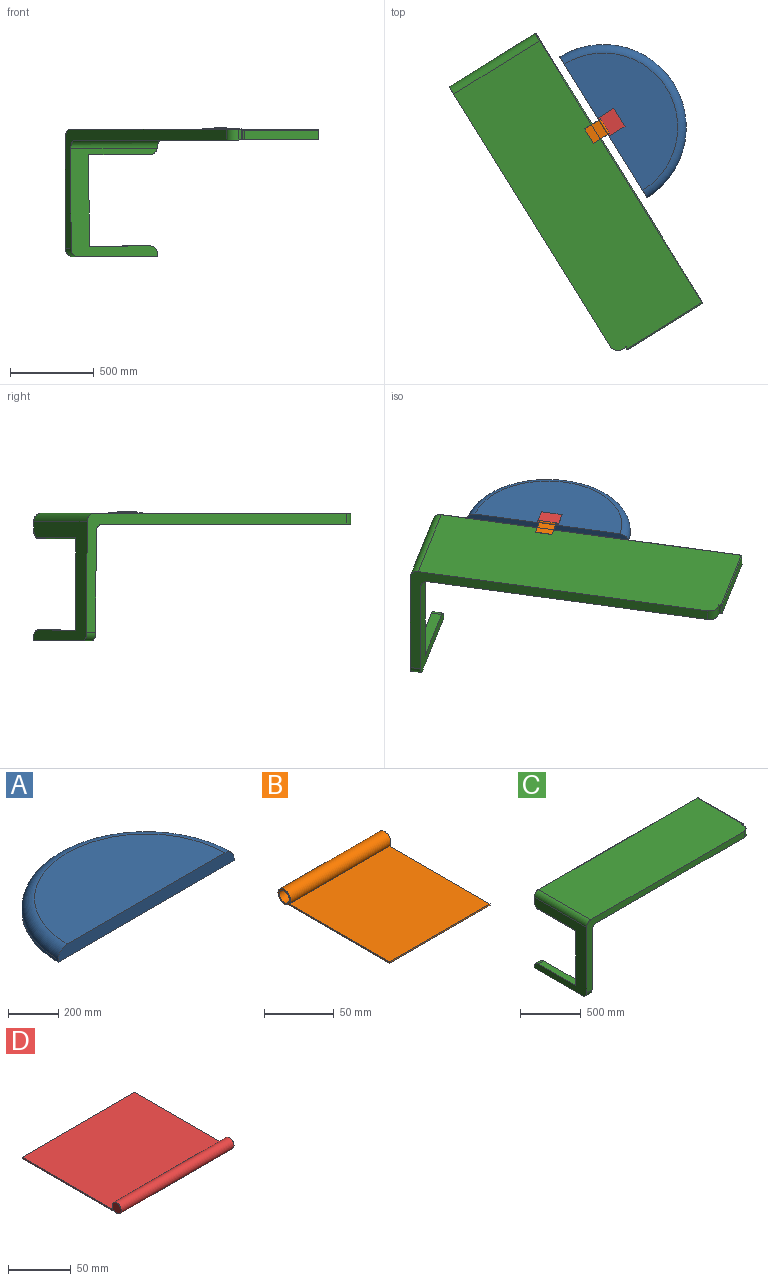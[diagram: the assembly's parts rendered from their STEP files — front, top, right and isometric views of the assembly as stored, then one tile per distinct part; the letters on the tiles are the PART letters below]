
ASSEMBLY  parts=4 mates=3
PART A: 5 faces, bbox 1072.2x536.1x63.5 mm
  f0: plane 990.6x63.5mm, normal (0,-1,0), area 61795.5mm2, adj f1,f2,f3,f4
  f1: cylinder r=495.3mm len=990.6mm, axis (0,0,1), area 19761.6mm2, adj f0,f2,f4
  f2: plane 990.6x495.3mm, normal (0,0,-1), area 385351mm2, adj f0,f1
  f3: plane 889x444.5mm, normal (0,0,1), area 310358.3mm2, adj f0,f4
  f4: torus R=444.5mm, axis (0,0,1), area 119538.1mm2, adj f0,f1,f3
PART B: 7 faces, bbox 101.6x113x12.7 mm
  f0: plane 101.6x101.6mm, normal (0,0,1), area 10322.6mm2, adj f1,f4,f5,f6
  f1: plane 101.6x1.27mm, normal (0,-1,0), area 129mm2, adj f0,f2,f5,f6
  f2: plane 102.87x101.6mm, normal (0,0,-1), area 10451.6mm2, adj f1,f4,f5,f6
  f3: cylinder r=5.08mm len=101.6mm, axis (1,0,0), area 3242.9mm2, adj f5,f6
  f4: cylinder r=6.35mm len=101.6mm, axis (1,0,0), area 3870.6mm2, adj f0,f2,f5,f6
  f5: plane 113.03x12.7mm, normal (-1,0,0), area 175.4mm2, adj f0,f1,f2,f3,f4
  f6: plane 113.03x12.7mm, normal (1,0,0), area 175.4mm2, adj f0,f1,f2,f3,f4
PART C: 33 faces, bbox 1902.8x613.8x766.2 mm
  f0: plane 63.5x30.48mm, normal (1,0,0), area 1618.4mm2, adj f6,f7,f13,f20,f32
  f1: plane 647.7x609.6mm, normal (1,0,0), area 129635.4mm2, adj f3,f4,f5,f10,f14,f15,f16,f17
  f2: plane 711.2x609.6mm, normal (-1,0,0), area 165501.5mm2, adj f3,f4,f8,f10,f15,f16,f18,f19
  f3: plane 63.5x12.7mm, normal (0,1,0), area 806.5mm2, adj f1,f2,f4,f18
  f4: plane 558.8x63.5mm, normal (0,0,-1), area 35483.8mm2, adj f1,f2,f3,f19
  f5: cylinder r=50.8mm len=609.6mm, axis (0,-1,0), area 48637.1mm2, adj f1,f6,f9,f10,f17
  f6: plane 1784.35x609.6mm, normal (0,0,-1), area 1085216.6mm2, adj f0,f5,f9,f10,f12,f13,f20,f21
  f7: plane 1842.77x604.52mm, normal (0,0,1), area 1112302mm2, adj f0,f8,f10,f13,f28,f30,f32
  f8: cylinder r=50.8mm len=604.52mm, axis (0,-1,0), area 48238.6mm2, adj f2,f7,f10,f27
  f9: plane 1888.49x96.52mm, normal (0,1,0), area 112649.8mm2, adj f5,f6,f17,f23,f26,f27,f28
  f10: plane 1828.8x711.2mm, normal (0,-1,0), area 157257.8mm2, adj f1,f2,f5,f6,f7,f8,f13,f19
  f11: cone r=0mm half-angle=59deg, axis (0,0,-1), area 591.1mm2, adj f12
  f12: cylinder r=12.7mm len=25.4mm, axis (0,0,-1), area 1013.4mm2, adj f6,f11
  f13: cylinder r=50.8mm len=63.5mm, axis (0,0,1), area 5067.1mm2, adj f0,f6,f7,f10
  f14: plane 431.8x58.42mm, normal (0,0,-1), area 25225.8mm2, adj f1,f16,f17,f24
  f15: plane 431.8x63.5mm, normal (0,0,1), area 27419.3mm2, adj f1,f2,f16,f18
  f16: plane 551.18x63.5mm, normal (0,1,0), area 34682.9mm2, adj f1,f2,f14,f15,f24
  f17: cylinder r=50.8mm len=60.03mm, axis (1,0,0), area 4668.5mm2, adj f1,f5,f9,f14,f25
  f18: cylinder r=50.8mm len=63.5mm, axis (-1,0,0), area 5067.1mm2, adj f1,f2,f3,f15
  f19: cylinder r=50.8mm len=63.5mm, axis (1,0,0), area 5067.1mm2, adj f1,f2,f4,f10
  f20: plane 58.42x13.97mm, normal (0,-1,0), area 816.1mm2, adj f0,f6,f22,f32
  f21: plane 523.24x58.42mm, normal (1,0,0), area 30567.7mm2, adj f6,f22,f23,f30
  f22: cylinder r=5.08mm len=58.42mm, axis (0,0,1), area 466.2mm2, adj f6,f20,f21,f31
  f23: cylinder r=5.08mm len=58.42mm, axis (0,0,-1), area 466.2mm2, adj f6,f9,f21,f29
  f24: cylinder r=5.08mm len=431.8mm, axis (0,-1,0), area 3445.6mm2, adj f2,f14,f16,f25
  f25: torus R=45.72mm, axis (-1,0,0), area 613.6mm2, adj f2,f17,f24,f26
  f26: cylinder r=5.08mm len=50.8mm, axis (0,0,1), area 405.4mm2, adj f2,f9,f25,f27
  f27: torus R=45.72mm, axis (0,-1,0), area 613.6mm2, adj f8,f9,f26,f28
  f28: cylinder r=5.08mm len=1842.77mm, axis (1,0,0), area 14704.7mm2, adj f7,f9,f27,f29
  f29: sphere r=5.08mm, area 40.5mm2, adj f23,f28,f30
  f30: cylinder r=5.08mm len=523.24mm, axis (0,-1,0), area 4175.3mm2, adj f7,f21,f29,f31
  f31: sphere r=5.08mm, area 40.5mm2, adj f22,f30,f32
  f32: cylinder r=5.08mm len=13.97mm, axis (1,0,0), area 111.5mm2, adj f0,f7,f20,f31
PART D: 13 faces, bbox 127x111.8x10.2 mm
  f0: plane 12.7x0.96mm, normal (0,0.66,0.75), area 16.2mm2, adj f3,f5,f7,f9
  f1: plane 127x1.63mm, normal (0,-0.64,-0.77), area 139.4mm2, adj f5,f6,f7,f8,f9,f10,f11,f12
  f2: plane 127x1.27mm, normal (0,1,0), area 161.3mm2, adj f3,f6,f7,f8
  f3: plane 127x101.6mm, normal (0,0,1), area 12903.2mm2, adj f0,f2,f4,f7,f8,f12
  f4: plane 12.7x0.96mm, normal (0,0.66,0.75), area 16.2mm2, adj f3,f5,f8,f11
  f5: cylinder r=5.08mm len=127mm, axis (1,0,0), area 3924.7mm2, adj f0,f1,f4,f7,f8,f10
  f6: plane 127x101.6mm, normal (0,0,-1), area 12903.2mm2, adj f1,f2,f7,f8
  f7: plane 111.76x10.16mm, normal (-1,0,0), area 211.8mm2, adj f0,f1,f2,f3,f5,f6
  f8: plane 111.76x10.16mm, normal (1,0,0), area 211.8mm2, adj f1,f2,f3,f4,f5,f6
  f9: plane 1.63x1.58mm, normal (1,0,0), area 1.3mm2, adj f0,f1,f10,f12
  f10: plane 101.6x0.76mm, normal (0,0.75,-0.66), area 102.9mm2, adj f1,f5,f9,f11
  f11: plane 1.63x1.58mm, normal (-1,0,0), area 1.3mm2, adj f1,f4,f10,f12
  f12: plane 101.6x0.74mm, normal (0,-0.75,0.66), area 99.5mm2, adj f1,f3,f9,f11
PLACE A rot(axis=(0,0,-1),58.2deg) t=(-1031.78,741.43,0.52)mm
PLACE B rot(axis=(0,0,-1),58.2deg) t=(-1084.37,649.05,22.25)mm
PLACE C rot(axis=(0,0,-1),58.2deg) t=(-963.88,-614.58,-0.85)mm
PLACE D rot(axis=(0,0,-1),58.2deg) t=(-993.41,690.51,-21.61)mm
MATE revolute D.f5 <-> B.f3  axis (0.53,-0.85,0) through (-993.41,690.51,5.6)mm
MATE parallel D.f6 <-> A.f3  axis (0,0,-1) through (-979.38,773.92,0.52)mm
MATE parallel B.f2 <-> C.f7  axis (0,0,-1) through (-1073.82,715.36,0.41)mm
